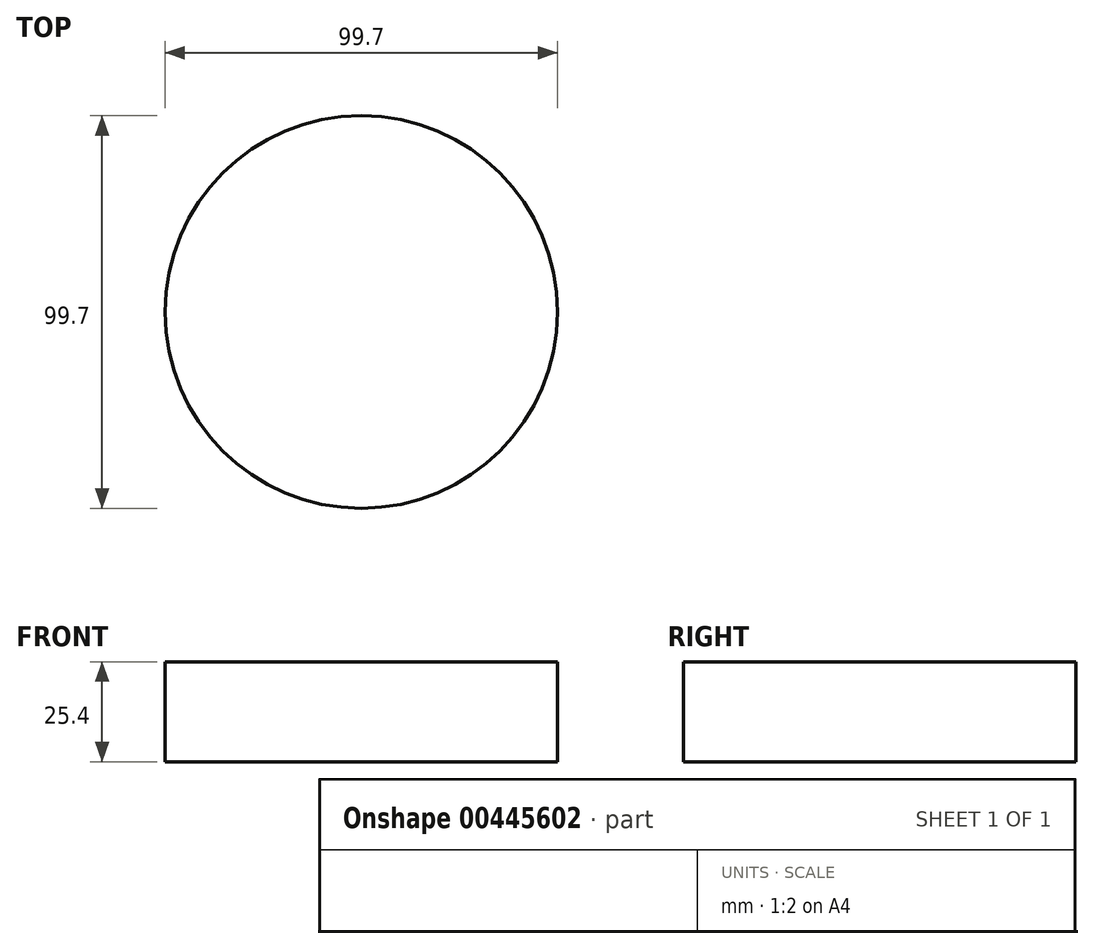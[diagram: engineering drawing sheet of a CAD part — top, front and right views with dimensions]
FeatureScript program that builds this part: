
annotation { "Feature Type Name" : "Feature", "Feature Type Description" : "" }
export const myFeature = defineFeature(function(context is Context, id is Id, definition is map)
    precondition{}
    {
        {
            var Q0;
            Q0=qCreatedBy(makeId("Top.planeOp"),FACE);
            var sketch = newSketch(context, id + "F0", { "sketchPlane" : qUnion([Q0])});
            skCircle(sketch, "E0", {"center": v(0, 0) * mm, "radius": 49.85 * mm});
            skSolve(sketch);
        }
        {
            var Q0;
            Q0 = qSketchRegion(id + "F0", true);
            extrude(context, id + "F1", {"entities" : qUnion([Q0]), "depth" : 25.4 * mm});
        }
    });
